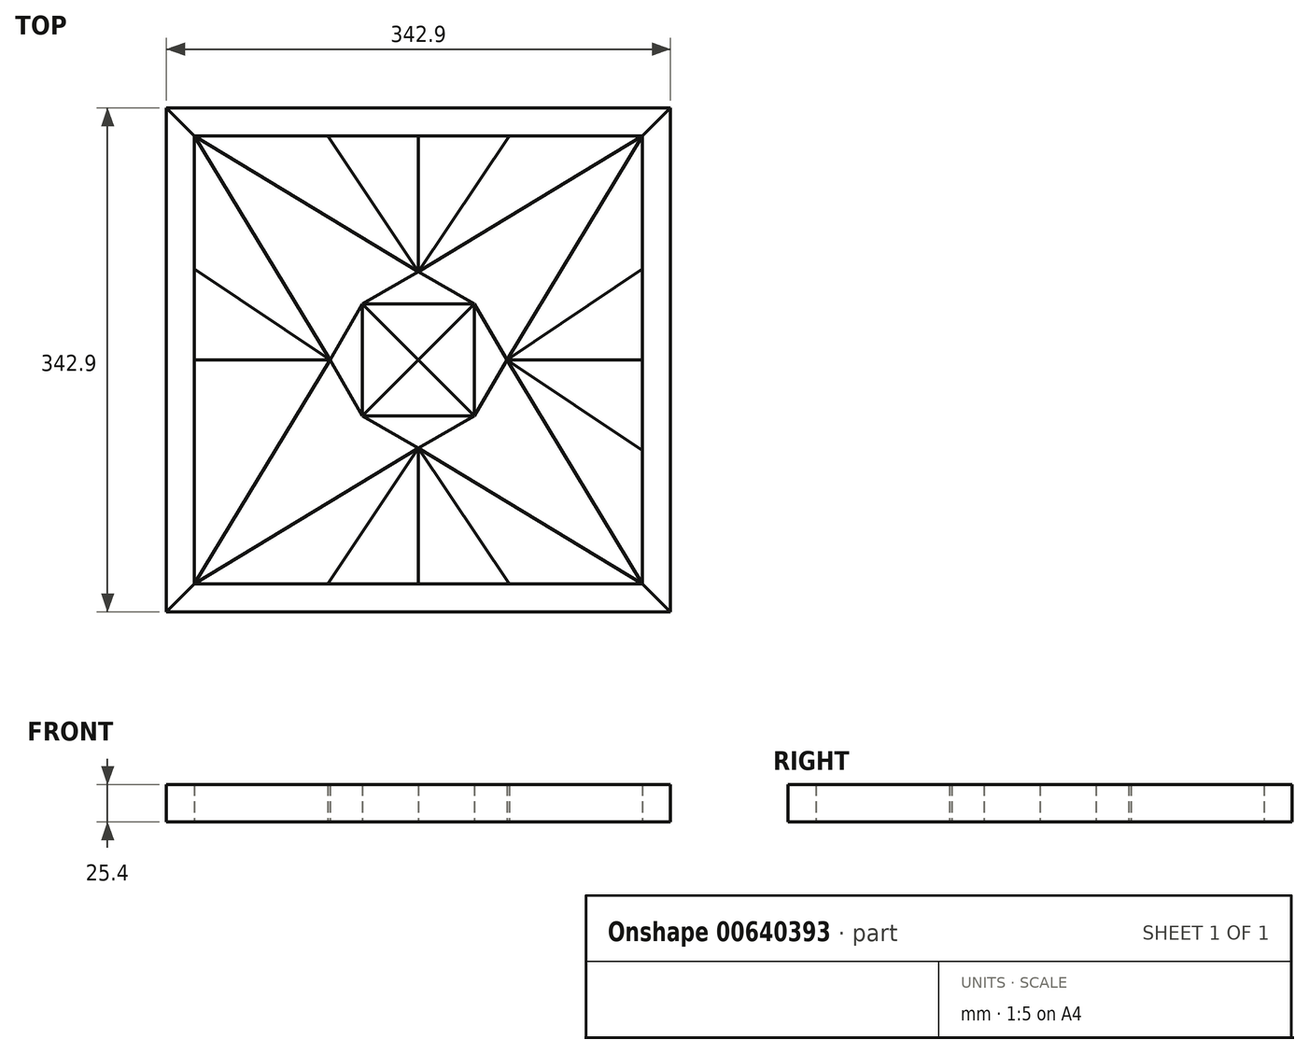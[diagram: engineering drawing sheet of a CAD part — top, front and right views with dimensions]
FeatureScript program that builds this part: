
annotation { "Feature Type Name" : "Feature", "Feature Type Description" : "" }
export const myFeature = defineFeature(function(context is Context, id is Id, definition is map)
    precondition{}
    {
        {
            var Q0;
            Q0=qCreatedBy(makeId("Top.planeOp"),FACE);
            var sketch = newSketch(context, id + "F0", { "sketchPlane" : qUnion([Q0])});
            skLineSegment(sketch, "E0.bottom", {"start": v(-171.45, 171.45) * mm, "end": v(171.45, 171.45) * mm});
            skLineSegment(sketch, "E0.top", {"start": v(-171.45, -171.45) * mm, "end": v(171.45, -171.45) * mm});
            skLineSegment(sketch, "E0.left", {"start": v(-171.45, 171.45) * mm, "end": v(-171.45, -171.45) * mm});
            skLineSegment(sketch, "E0.right", {"start": v(171.45, 171.45) * mm, "end": v(171.45, -171.45) * mm});
            skPoint(sketch, "E0.middle", {"position": v(0, 0) * mm});
            skSolve(sketch);
        }
        {
            var Q0;
            Q0=makeQuery(id+"F0.imprint","IMPRINT",FACE,{"disambiguationData":[TD([[makeQuery(id+"F0.imprint","IMPRINT",EDGE,{"derivedFrom":sQuery(id+"F0.wireOp",EDGE,"E0.bottom")}),-1.0]])]});
            var sketch = newSketch(context, id + "F1", { "sketchPlane" : qUnion([Q0])});
            skLineSegment(sketch, "E1.bottom", {"start": v(-152.4, 152.4) * mm, "end": v(152.4, 152.4) * mm});
            skLineSegment(sketch, "E1.top", {"start": v(-152.4, -152.4) * mm, "end": v(152.4, -152.4) * mm});
            skLineSegment(sketch, "E1.left", {"start": v(-152.4, 152.4) * mm, "end": v(-152.4, -152.4) * mm});
            skLineSegment(sketch, "E1.right", {"start": v(152.4, 152.4) * mm, "end": v(152.4, -152.4) * mm});
            skPoint(sketch, "E1.middle", {"position": v(0, 0) * mm});
            skSolve(sketch);
        }
        {
            var Q0;
            Q0=makeQuery(id+"F0.imprint","IMPRINT",FACE,{"disambiguationData":[TD([[makeQuery(id+"F0.imprint","IMPRINT",EDGE,{"derivedFrom":sQuery(id+"F0.wireOp",EDGE,"E0.bottom")}),-1.0]])]});
            var sketch = newSketch(context, id + "F2", { "sketchPlane" : qUnion([Q0])});
            skLineSegment(sketch, "E2.bottom", {"start": v(-38.1, 38.1) * mm, "end": v(38.1, 38.1) * mm});
            skLineSegment(sketch, "E2.top", {"start": v(-38.1, -38.1) * mm, "end": v(38.1, -38.1) * mm});
            skLineSegment(sketch, "E2.left", {"start": v(-38.1, 38.1) * mm, "end": v(-38.1, -38.1) * mm});
            skLineSegment(sketch, "E2.right", {"start": v(38.1, 38.1) * mm, "end": v(38.1, -38.1) * mm});
            skPoint(sketch, "E2.middle", {"position": v(0, 0) * mm});
            skLineSegment(sketch, "E3", {"start": v(38.1, -38.1) * mm, "end": v(-38.1, 38.1) * mm});
            skLineSegment(sketch, "E4", {"start": v(-38.1, -38.1) * mm, "end": v(38.1, 38.1) * mm});
            skSolve(sketch);
        }
        {
            var Q0;
            Q0=makeQuery(id+"F1.imprint","IMPRINT",FACE,{"disambiguationData":[TD([[makeQuery(id+"F1.imprint","IMPRINT",EDGE,{"derivedFrom":sQuery(id+"F1.wireOp",EDGE,"E1.bottom")}),-1.0]])]});
            var sketch = newSketch(context, id + "F3", { "sketchPlane" : qUnion([Q0])});
            skLineSegment(sketch, "E5.0", {"start": v(-38.1, 38.1) * mm, "end": v(38.1, 38.1) * mm});
            skLineSegment(sketch, "E6.0", {"start": v(-38.1, 38.1) * mm, "end": v(-38.1, -38.1) * mm});
            skPoint(sketch, "E7.0", {"position": v(0, -38.1) * mm});
            skLineSegment(sketch, "E8.0", {"start": v(-38.1, -38.1) * mm, "end": v(38.1, -38.1) * mm});
            skLineSegment(sketch, "E9.0", {"start": v(38.1, 38.1) * mm, "end": v(38.1, -38.1) * mm});
            skLineSegment(sketch, "E10", {"start": v(-38.1, 38.1) * mm, "end": v(0, 60.1) * mm});
            skLineSegment(sketch, "E11", {"start": v(0, 60.1) * mm, "end": v(38.1, 38.1) * mm});
            skLineSegment(sketch, "E12", {"start": v(38.1, 38.1) * mm, "end": v(60.1, 0) * mm});
            skLineSegment(sketch, "E13", {"start": v(60.1, 0) * mm, "end": v(38.1, -38.1) * mm});
            skLineSegment(sketch, "E14", {"start": v(38.1, -38.1) * mm, "end": v(0, -60.1) * mm});
            skLineSegment(sketch, "E15", {"start": v(0, -60.1) * mm, "end": v(-38.1, -38.1) * mm});
            skLineSegment(sketch, "E16", {"start": v(-60.1, 0) * mm, "end": v(-38.1, 38.1) * mm});
            skLineSegment(sketch, "E17", {"start": v(-38.1, -38.1) * mm, "end": v(-60.1, 0) * mm});
            skSolve(sketch);
        }
        {
            var Q0;
            {var subQ0=sQuery(id+"F2.wireOp",EDGE,"E2.bottom");Q0=makeQuery(id+"F2.imprint","IMPRINT",FACE,{"disambiguationData":[TD([[makeQuery(id+"F2.imprint","IMPRINT",EDGE,{"derivedFrom":subQ0}),-1.0]])]});}
            extrude(context, id + "F4", {"entities" : qUnion([Q0]), "depth" : 25.4 * mm, "offsetDistance" : 25.4 * mm});
        }
        {
            var Q0;
            {var subQ0=sQuery(id+"F2.wireOp",EDGE,"E2.left");Q0=makeQuery(id+"F2.imprint","IMPRINT",FACE,{"disambiguationData":[TD([[makeQuery(id+"F2.imprint","IMPRINT",EDGE,{"derivedFrom":subQ0}),1.0]])]});}
            extrude(context, id + "F5", {"entities" : qUnion([Q0]), "depth" : 25.4 * mm, "offsetDistance" : 25.4 * mm});
        }
        {
            var Q0;
            {var subQ0=sQuery(id+"F2.wireOp",EDGE,"E2.top");Q0=makeQuery(id+"F2.imprint","IMPRINT",FACE,{"disambiguationData":[TD([[makeQuery(id+"F2.imprint","IMPRINT",EDGE,{"derivedFrom":subQ0}),1.0]])]});}
            extrude(context, id + "F6", {"entities" : qUnion([Q0]), "depth" : 25.4 * mm, "offsetDistance" : 25.4 * mm});
        }
        {
            var Q0;
            {var subQ0=sQuery(id+"F2.wireOp",EDGE,"E2.right");Q0=makeQuery(id+"F2.imprint","IMPRINT",FACE,{"disambiguationData":[TD([[makeQuery(id+"F2.imprint","IMPRINT",EDGE,{"derivedFrom":subQ0}),-1.0]])]});}
            extrude(context, id + "F7", {"entities" : qUnion([Q0]), "depth" : 25.4 * mm, "offsetDistance" : 25.4 * mm});
        }
        {
            var Q0;
            Q0=makeQuery(id+"F3.imprint","IMPRINT",FACE,{"disambiguationData":[TD([[makeQuery(id+"F3.imprint","IMPRINT",EDGE,{"derivedFrom":sQuery(id+"F3.wireOp",EDGE,"E5.0")}),1.0]])]});
            extrude(context, id + "F8", {"entities" : qUnion([Q0]), "depth" : 25.4 * mm, "offsetDistance" : 25.4 * mm});
        }
        {
            var Q0;
            Q0=makeQuery(id+"F3.imprint","IMPRINT",FACE,{"disambiguationData":[TD([[makeQuery(id+"F3.imprint","IMPRINT",EDGE,{"derivedFrom":sQuery(id+"F3.wireOp",EDGE,"E6.0")}),-1.0]])]});
            extrude(context, id + "F9", {"entities" : qUnion([Q0]), "depth" : 25.4 * mm, "offsetDistance" : 25.4 * mm});
        }
        {
            var Q0;
            Q0=makeQuery(id+"F3.imprint","IMPRINT",FACE,{"disambiguationData":[TD([[makeQuery(id+"F3.imprint","IMPRINT",EDGE,{"derivedFrom":sQuery(id+"F3.wireOp",EDGE,"E8.0")}),-1.0]])]});
            extrude(context, id + "F10", {"entities" : qUnion([Q0]), "depth" : 25.4 * mm, "offsetDistance" : 25.4 * mm});
        }
        {
            var Q0;
            Q0=makeQuery(id+"F3.imprint","IMPRINT",FACE,{"disambiguationData":[TD([[makeQuery(id+"F3.imprint","IMPRINT",EDGE,{"derivedFrom":sQuery(id+"F3.wireOp",EDGE,"E9.0")}),1.0]])]});
            extrude(context, id + "F11", {"entities" : qUnion([Q0]), "depth" : 25.4 * mm, "offsetDistance" : 25.4 * mm});
        }
        {
            var Q0;
            Q0=makeQuery(id+"F2.imprint","IMPRINT",FACE,{"disambiguationData":[TD([[makeQuery(id+"F2.imprint","IMPRINT",EDGE,{"derivedFrom":sQuery(id+"F2.wireOp",EDGE,"E2.bottom")}),1.0]])]});
            var sketch = newSketch(context, id + "F12", { "sketchPlane" : qUnion([Q0])});
            skPoint(sketch, "E18.0", {"position": v(-152.4, 152.4) * mm});
            skPoint(sketch, "E19.0", {"position": v(-60.1, 0) * mm});
            skPoint(sketch, "E20.0", {"position": v(-38.1, 38.1) * mm});
            skPoint(sketch, "E21.0", {"position": v(0, 60.1) * mm});
            skPoint(sketch, "E22.0", {"position": v(38.1, 38.1) * mm});
            skPoint(sketch, "E23.0", {"position": v(60.1, 0) * mm});
            skPoint(sketch, "E24.0", {"position": v(38.1, -38.1) * mm});
            skPoint(sketch, "E25.0", {"position": v(0, -60.1) * mm});
            skPoint(sketch, "E26.0", {"position": v(-38.1, -38.1) * mm});
            skPoint(sketch, "E27.0", {"position": v(152.4, 152.4) * mm});
            skPoint(sketch, "E28.0", {"position": v(152.4, -152.4) * mm});
            skPoint(sketch, "E29.0", {"position": v(-152.4, -152.4) * mm});
            skLineSegment(sketch, "E30", {"start": v(0, 60.1) * mm, "end": v(-152.4, 152.4) * mm});
            skLineSegment(sketch, "E31", {"start": v(-60.1, 0) * mm, "end": v(-152.4, 152.4) * mm});
            skLineSegment(sketch, "E32", {"start": v(0, 60.1) * mm, "end": v(152.4, 152.4) * mm});
            skLineSegment(sketch, "E33", {"start": v(60.1, 0) * mm, "end": v(152.4, 152.4) * mm});
            skLineSegment(sketch, "E34", {"start": v(60.1, 0) * mm, "end": v(152.4, -152.4) * mm});
            skLineSegment(sketch, "E35", {"start": v(0, -60.1) * mm, "end": v(152.4, -152.4) * mm});
            skLineSegment(sketch, "E36", {"start": v(0, -60.1) * mm, "end": v(-152.4, -152.4) * mm});
            skLineSegment(sketch, "E37", {"start": v(-60.1, 0) * mm, "end": v(-152.4, -152.4) * mm});
            skLineSegment(sketch, "E38.0", {"start": v(-38.1, 38.1) * mm, "end": v(0, 60.1) * mm});
            skLineSegment(sketch, "E39.0", {"start": v(-60.1, 0) * mm, "end": v(-38.1, 38.1) * mm});
            skLineSegment(sketch, "E40.0", {"start": v(-38.1, -38.1) * mm, "end": v(-60.1, 0) * mm});
            skLineSegment(sketch, "E41.0", {"start": v(0, -60.1) * mm, "end": v(-38.1, -38.1) * mm});
            skLineSegment(sketch, "E42.0", {"start": v(38.1, -38.1) * mm, "end": v(0, -60.1) * mm});
            skLineSegment(sketch, "E43.0", {"start": v(60.1, 0) * mm, "end": v(38.1, -38.1) * mm});
            skLineSegment(sketch, "E44.0", {"start": v(38.1, 38.1) * mm, "end": v(60.1, 0) * mm});
            skLineSegment(sketch, "E45.0", {"start": v(0, 60.1) * mm, "end": v(38.1, 38.1) * mm});
            skSolve(sketch);
        }
        {
            var Q0;
            Q0=makeQuery(id+"F12.imprint","IMPRINT",FACE,{"disambiguationData":[TD([[makeQuery(id+"F12.imprint","IMPRINT",EDGE,{"derivedFrom":sQuery(id+"F12.wireOp",EDGE,"E30")}),1.0]])]});
            var Q1;
            Q1=makeQuery(id+"F12.imprint","IMPRINT",FACE,{"disambiguationData":[TD([[makeQuery(id+"F12.imprint","IMPRINT",EDGE,{"derivedFrom":sQuery(id+"F12.wireOp",EDGE,"E32")}),-1.0]])]});
            var Q2;
            Q2=makeQuery(id+"F12.imprint","IMPRINT",FACE,{"disambiguationData":[TD([[makeQuery(id+"F12.imprint","IMPRINT",EDGE,{"derivedFrom":sQuery(id+"F12.wireOp",EDGE,"E36")}),-1.0]])]});
            var Q3;
            Q3=makeQuery(id+"F12.imprint","IMPRINT",FACE,{"disambiguationData":[TD([[makeQuery(id+"F12.imprint","IMPRINT",EDGE,{"derivedFrom":sQuery(id+"F12.wireOp",EDGE,"E34")}),-1.0]])]});
            extrude(context, id + "F13", {"entities" : qUnion([Q0, Q1, Q2, Q3]), "depth" : 25.4 * mm, "offsetDistance" : 25.4 * mm});
        }
        {
            var Q0;
            Q0=makeQuery(id+"F0.imprint","IMPRINT",FACE,{"disambiguationData":[TD([[makeQuery(id+"F0.imprint","IMPRINT",EDGE,{"derivedFrom":sQuery(id+"F0.wireOp",EDGE,"E0.bottom")}),-1.0]])]});
            var sketch = newSketch(context, id + "F14", { "sketchPlane" : qUnion([Q0])});
            skPoint(sketch, "E46.0", {"position": v(-152.4, 152.4) * mm});
            skPoint(sketch, "E47.0", {"position": v(-60.1, 0) * mm});
            skPoint(sketch, "E48.0", {"position": v(-152.4, -152.4) * mm});
            skPoint(sketch, "E49.0", {"position": v(152.4, 152.4) * mm});
            skPoint(sketch, "E50.0", {"position": v(0, 60.1) * mm});
            skPoint(sketch, "E51.0", {"position": v(152.4, -152.4) * mm});
            skPoint(sketch, "E52.0", {"position": v(60.1, 0) * mm});
            skPoint(sketch, "E53.0", {"position": v(0, -60.1) * mm});
            skLineSegment(sketch, "E54.0", {"start": v(-152.4, 152.4) * mm, "end": v(-152.4, -152.4) * mm});
            skLineSegment(sketch, "E55.0", {"start": v(-152.4, 152.4) * mm, "end": v(152.4, 152.4) * mm});
            skLineSegment(sketch, "E56.0", {"start": v(152.4, 152.4) * mm, "end": v(152.4, -152.4) * mm});
            skLineSegment(sketch, "E57.0", {"start": v(-152.4, -152.4) * mm, "end": v(152.4, -152.4) * mm});
            skLineSegment(sketch, "E58.0", {"start": v(0, -60.1) * mm, "end": v(-152.4, -152.4) * mm});
            skLineSegment(sketch, "E59.0", {"start": v(0, -60.1) * mm, "end": v(152.4, -152.4) * mm});
            skLineSegment(sketch, "E60.0", {"start": v(-60.1, 0) * mm, "end": v(-152.4, -152.4) * mm});
            skLineSegment(sketch, "E61.0", {"start": v(-60.1, 0) * mm, "end": v(-152.4, 152.4) * mm});
            skLineSegment(sketch, "E62.0", {"start": v(0, 60.1) * mm, "end": v(-152.4, 152.4) * mm});
            skLineSegment(sketch, "E63.0", {"start": v(0, 60.1) * mm, "end": v(152.4, 152.4) * mm});
            skLineSegment(sketch, "E64.0", {"start": v(60.1, 0) * mm, "end": v(152.4, 152.4) * mm});
            skLineSegment(sketch, "E65.0", {"start": v(60.1, 0) * mm, "end": v(152.4, -152.4) * mm});
            skLineSegment(sketch, "E66", {"start": v(0, -60.1) * mm, "end": v(-61.79, -152.4) * mm});
            skLineSegment(sketch, "E67", {"start": v(0, -60.1) * mm, "end": v(61.79, -152.4) * mm});
            skLineSegment(sketch, "E68", {"start": v(0, -60.1) * mm, "end": v(0, -152.4) * mm});
            skLineSegment(sketch, "E69", {"start": v(-60.1, 0) * mm, "end": v(-152.4, 61.79) * mm});
            skLineSegment(sketch, "E70", {"start": v(-60.1, 0) * mm, "end": v(-152.4, -61.79) * mm});
            skLineSegment(sketch, "E71", {"start": v(-60.1, 0) * mm, "end": v(-152.4, 0) * mm});
            skLineSegment(sketch, "E72", {"start": v(0, 60.1) * mm, "end": v(-61.79, 152.4) * mm});
            skLineSegment(sketch, "E73", {"start": v(0, 60.1) * mm, "end": v(0, 152.4) * mm});
            skLineSegment(sketch, "E74", {"start": v(0, 60.1) * mm, "end": v(61.79, 152.4) * mm});
            skLineSegment(sketch, "E75", {"start": v(60.1, 0) * mm, "end": v(152.4, 61.79) * mm});
            skLineSegment(sketch, "E76", {"start": v(60.1, 0) * mm, "end": v(152.4, -61.79) * mm});
            skLineSegment(sketch, "E77", {"start": v(60.1, 0) * mm, "end": v(152.4, 0) * mm});
            skSolve(sketch);
        }
        {
            var Q0;
            {var subQ0=sQuery(id+"F14.wireOp",EDGE,"E58.0");Q0=makeQuery(id+"F14.imprint","IMPRINT",FACE,{"disambiguationData":[TD([[makeQuery(id+"F14.imprint","IMPRINT",EDGE,{"derivedFrom":subQ0}),1.0]])]});}
            var Q1;
            {var subQ0=sQuery(id+"F14.wireOp",EDGE,"E69");Q1=makeQuery(id+"F14.imprint","IMPRINT",FACE,{"disambiguationData":[TD([[makeQuery(id+"F14.imprint","IMPRINT",EDGE,{"derivedFrom":subQ0}),1.0]])]});}
            var Q2;
            {var subQ0=sQuery(id+"F14.wireOp",EDGE,"E62.0");Q2=makeQuery(id+"F14.imprint","IMPRINT",FACE,{"disambiguationData":[TD([[makeQuery(id+"F14.imprint","IMPRINT",EDGE,{"derivedFrom":subQ0}),-1.0]])]});}
            var Q3;
            {var subQ0=sQuery(id+"F14.wireOp",EDGE,"E73");Q3=makeQuery(id+"F14.imprint","IMPRINT",FACE,{"disambiguationData":[TD([[makeQuery(id+"F14.imprint","IMPRINT",EDGE,{"derivedFrom":subQ0}),-1.0]])]});}
            var Q4;
            {var subQ0=sQuery(id+"F14.wireOp",EDGE,"E75");Q4=makeQuery(id+"F14.imprint","IMPRINT",FACE,{"disambiguationData":[TD([[makeQuery(id+"F14.imprint","IMPRINT",EDGE,{"derivedFrom":subQ0}),-1.0]])]});}
            var Q5;
            {var subQ0=sQuery(id+"F14.wireOp",EDGE,"E65.0");Q5=makeQuery(id+"F14.imprint","IMPRINT",FACE,{"disambiguationData":[TD([[makeQuery(id+"F14.imprint","IMPRINT",EDGE,{"derivedFrom":subQ0}),1.0]])]});}
            var Q6;
            {var subQ0=sQuery(id+"F14.wireOp",EDGE,"E59.0");Q6=makeQuery(id+"F14.imprint","IMPRINT",FACE,{"disambiguationData":[TD([[makeQuery(id+"F14.imprint","IMPRINT",EDGE,{"derivedFrom":subQ0}),-1.0]])]});}
            extrude(context, id + "F15", {"entities" : qUnion([Q0, Q1, Q2, Q3, Q4, Q5, Q6]), "depth" : 25.4 * mm, "offsetDistance" : 25.4 * mm});
        }
        {
            var Q0;
            {var subQ0=sQuery(id+"F14.wireOp",EDGE,"E66");Q0=makeQuery(id+"F14.imprint","IMPRINT",FACE,{"disambiguationData":[TD([[makeQuery(id+"F14.imprint","IMPRINT",EDGE,{"derivedFrom":subQ0}),1.0]])]});}
            var Q1;
            {var subQ0=sQuery(id+"F14.wireOp",EDGE,"E60.0");Q1=makeQuery(id+"F14.imprint","IMPRINT",FACE,{"disambiguationData":[TD([[makeQuery(id+"F14.imprint","IMPRINT",EDGE,{"derivedFrom":subQ0}),-1.0]])]});}
            var Q2;
            {var subQ0=sQuery(id+"F14.wireOp",EDGE,"E72");Q2=makeQuery(id+"F14.imprint","IMPRINT",FACE,{"disambiguationData":[TD([[makeQuery(id+"F14.imprint","IMPRINT",EDGE,{"derivedFrom":subQ0}),-1.0]])]});}
            var Q3;
            {var subQ0=sQuery(id+"F14.wireOp",EDGE,"E76");Q3=makeQuery(id+"F14.imprint","IMPRINT",FACE,{"disambiguationData":[TD([[makeQuery(id+"F14.imprint","IMPRINT",EDGE,{"derivedFrom":subQ0}),1.0]])]});}
            var Q4;
            {var subQ0=sQuery(id+"F14.wireOp",EDGE,"E64.0");Q4=makeQuery(id+"F14.imprint","IMPRINT",FACE,{"disambiguationData":[TD([[makeQuery(id+"F14.imprint","IMPRINT",EDGE,{"derivedFrom":subQ0}),-1.0]])]});}
            var Q5;
            {var subQ0=sQuery(id+"F14.wireOp",EDGE,"E63.0");Q5=makeQuery(id+"F14.imprint","IMPRINT",FACE,{"disambiguationData":[TD([[makeQuery(id+"F14.imprint","IMPRINT",EDGE,{"derivedFrom":subQ0}),1.0]])]});}
            var Q6;
            {var subQ0=sQuery(id+"F14.wireOp",EDGE,"E61.0");Q6=makeQuery(id+"F14.imprint","IMPRINT",FACE,{"disambiguationData":[TD([[makeQuery(id+"F14.imprint","IMPRINT",EDGE,{"derivedFrom":subQ0}),1.0]])]});}
            var Q7;
            {var subQ0=sQuery(id+"F14.wireOp",EDGE,"E70");Q7=makeQuery(id+"F14.imprint","IMPRINT",FACE,{"disambiguationData":[TD([[makeQuery(id+"F14.imprint","IMPRINT",EDGE,{"derivedFrom":subQ0}),-1.0]])]});}
            extrude(context, id + "F16", {"entities" : qUnion([Q0, Q1, Q2, Q3, Q4, Q5, Q6, Q7]), "depth" : 25.4 * mm, "offsetDistance" : 25.4 * mm});
        }
        {
            var Q0;
            {var subQ0=sQuery(id+"F14.wireOp",EDGE,"E67");Q0=makeQuery(id+"F14.imprint","IMPRINT",FACE,{"disambiguationData":[TD([[makeQuery(id+"F14.imprint","IMPRINT",EDGE,{"derivedFrom":subQ0}),-1.0]])]});}
            extrude(context, id + "F17", {"entities" : qUnion([Q0]), "depth" : 25.4 * mm, "offsetDistance" : 25.4 * mm});
        }
        {
            var Q0;
            Q0=makeQuery(id+"F14.imprint","IMPRINT",FACE,{"disambiguationData":[TD([[makeQuery(id+"F14.imprint","IMPRINT",EDGE,{"derivedFrom":makeQuery(id+"F0.imprint","IMPRINT",EDGE,{"derivedFrom":sQuery(id+"F0.wireOp",EDGE,"E0.bottom")})}),-1.0]])]});
            var sketch = newSketch(context, id + "F18", { "sketchPlane" : qUnion([Q0])});
            skPoint(sketch, "E78.0", {"position": v(-152.4, 152.4) * mm});
            skPoint(sketch, "E79.0", {"position": v(-171.45, 171.45) * mm});
            skPoint(sketch, "E80.0", {"position": v(171.45, 171.45) * mm});
            skPoint(sketch, "E81.0", {"position": v(152.4, 152.4) * mm});
            skPoint(sketch, "E82.0", {"position": v(152.4, -152.4) * mm});
            skPoint(sketch, "E83.0", {"position": v(171.45, -171.45) * mm});
            skPoint(sketch, "E84.0", {"position": v(-171.45, -171.45) * mm});
            skPoint(sketch, "E85.0", {"position": v(-152.4, -152.4) * mm});
            skLineSegment(sketch, "E86", {"start": v(-152.4, 152.4) * mm, "end": v(-171.45, 171.45) * mm});
            skLineSegment(sketch, "E87", {"start": v(152.4, 152.4) * mm, "end": v(171.45, 171.45) * mm});
            skLineSegment(sketch, "E88", {"start": v(152.4, -152.4) * mm, "end": v(171.45, -171.45) * mm});
            skLineSegment(sketch, "E89", {"start": v(-171.45, -171.45) * mm, "end": v(-152.4, -152.4) * mm});
            skLineSegment(sketch, "E90.0", {"start": v(-152.4, 152.4) * mm, "end": v(-152.4, -152.4) * mm});
            skLineSegment(sketch, "E91.0", {"start": v(-171.45, 171.45) * mm, "end": v(-171.45, -171.45) * mm});
            skLineSegment(sketch, "E92.0", {"start": v(152.4, 152.4) * mm, "end": v(152.4, -152.4) * mm});
            skLineSegment(sketch, "E93.0", {"start": v(171.45, 171.45) * mm, "end": v(171.45, -171.45) * mm});
            skSolve(sketch);
        }
        {
            var Q0;
            {var subQ1=sQuery(id+"F18.wireOp",EDGE,"E86");Q0=makeQuery(id+"F18.imprint","IMPRINT",FACE,{"disambiguationData":[TD([[makeQuery(id+"F18.imprint","IMPRINT",EDGE,{"derivedFrom":subQ1}),1.0]])]});}
            var Q1;
            {var subQ3=sQuery(id+"F18.wireOp",EDGE,"E87");Q1=makeQuery(id+"F18.imprint","IMPRINT",FACE,{"disambiguationData":[TD([[makeQuery(id+"F18.imprint","IMPRINT",EDGE,{"derivedFrom":subQ3}),-1.0]])]});}
            extrude(context, id + "F19", {"entities" : qUnion([Q0, Q1]), "depth" : 25.4 * mm, "offsetDistance" : 25.4 * mm});
        }
        {
            var Q0;
            Q0=makeQuery(id+"F18.imprint","IMPRINT",FACE,{"disambiguationData":[TD([[makeQuery(id+"F18.imprint","IMPRINT",EDGE,{"derivedFrom":sQuery(id+"F18.wireOp",EDGE,"E86")}),-1.0]])]});
            var Q1;
            Q1=makeQuery(id+"F18.imprint","IMPRINT",FACE,{"disambiguationData":[TD([[makeQuery(id+"F18.imprint","IMPRINT",EDGE,{"derivedFrom":sQuery(id+"F18.wireOp",EDGE,"E88")}),-1.0]])]});
            extrude(context, id + "F20", {"entities" : qUnion([Q0, Q1]), "depth" : 25.4 * mm, "offsetDistance" : 25.4 * mm});
        }
    });
